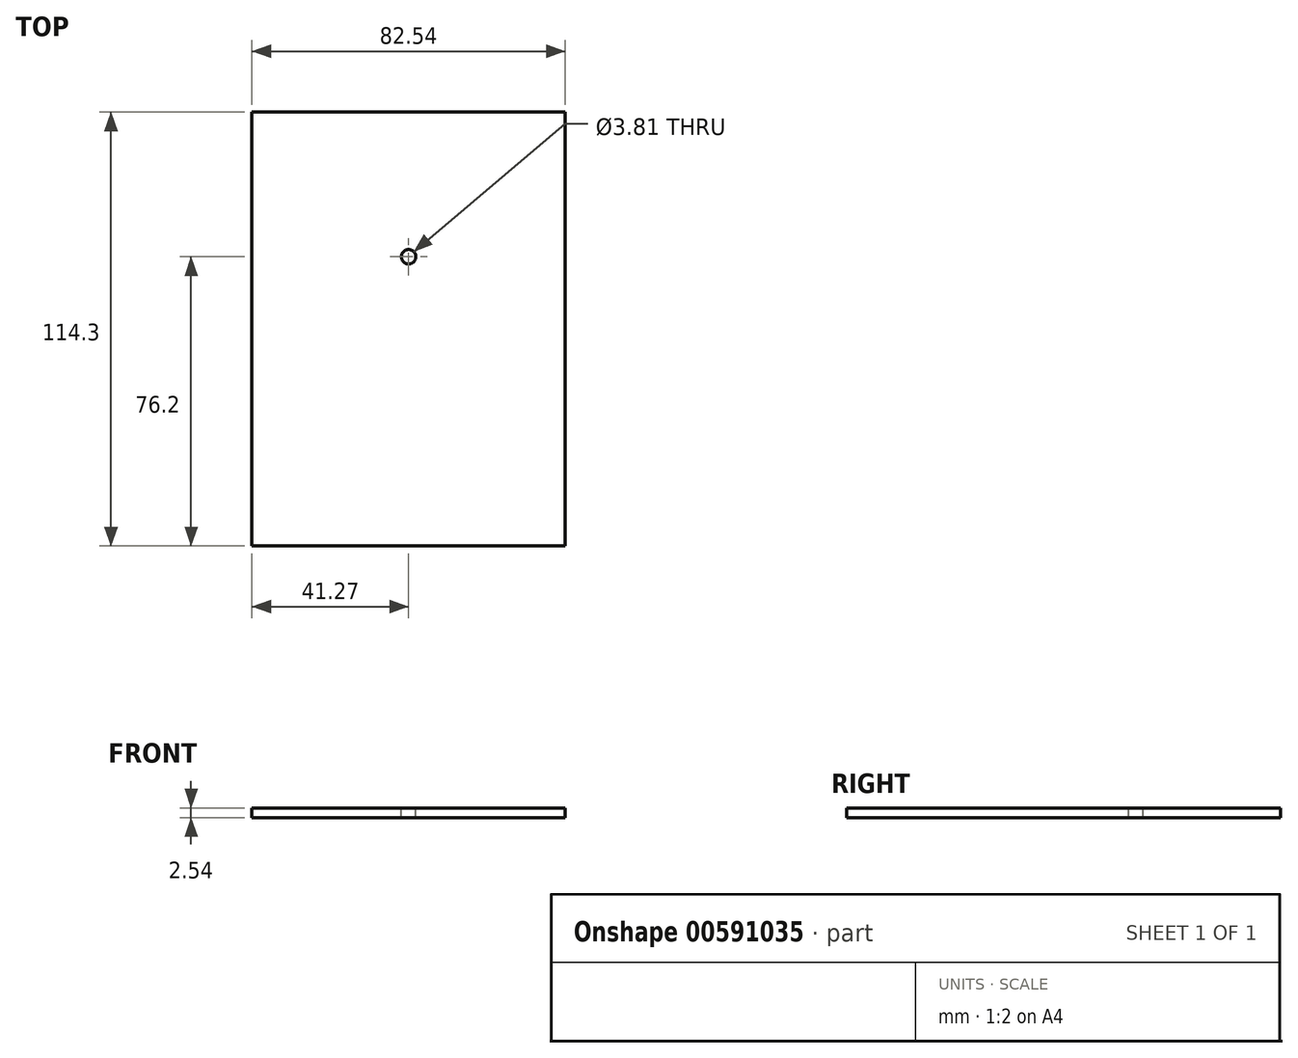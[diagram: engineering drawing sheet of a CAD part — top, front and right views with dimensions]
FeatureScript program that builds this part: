
annotation { "Feature Type Name" : "Feature", "Feature Type Description" : "" }
export const myFeature = defineFeature(function(context is Context, id is Id, definition is map)
    precondition{}
    {
        {
            var Q0;
            Q0=qCreatedBy(makeId("Top.planeOp"),FACE);
            var sketch = newSketch(context, id + "F0", { "sketchPlane" : qUnion([Q0])});
            skLineSegment(sketch, "E0.bottom", {"start": v(-41.28, 57.15) * mm, "end": v(41.27, 57.15) * mm});
            skLineSegment(sketch, "E0.top", {"start": v(-41.28, -57.15) * mm, "end": v(41.28, -57.15) * mm});
            skLineSegment(sketch, "E0.left", {"start": v(-41.28, 57.15) * mm, "end": v(-41.28, -57.15) * mm});
            skLineSegment(sketch, "E0.right", {"start": v(41.27, 57.15) * mm, "end": v(41.28, -57.15) * mm});
            skSolve(sketch);
        }
        {
            var Q0;
            Q0 = qSketchRegion(id + "F0", true);
            extrude(context, id + "F1", {"entities" : qUnion([Q0]), "depth" : 2.54 * mm, "offsetDistance" : 25.4 * mm});
        }
        {
            var Q0;
            Q0=makeQuery(id+"F1.opExtrude","CAP_FACE",FACE,{"disambiguationData":[OSD([sQuery(id+"F0.wireOp",EDGE,"E0.bottom"),sQuery(id+"F0.wireOp",EDGE,"E0.top"),sQuery(id+"F0.wireOp",EDGE,"E0.left"),sQuery(id+"F0.wireOp",EDGE,"E0.right")])],"isStart":false});
            var sketch = newSketch(context, id + "F2", { "sketchPlane" : qUnion([Q0])});
            skCircle(sketch, "E1", {"center": v(0, 19.05) * mm, "radius": 1.9 * mm});
            skSolve(sketch);
        }
        {
            var Q0;
            Q0 = qSketchRegion(id + "F2", true);
            extrude(context, id + "F3", {"entities" : qUnion([Q0]), "operationType" : NewBodyOperationType.REMOVE, "endBound" : BoundingType.THROUGH_ALL, "oppositeDirection" : true, "depth" : 25.4 * mm, "offsetDistance" : 25.4 * mm});
        }
    });
